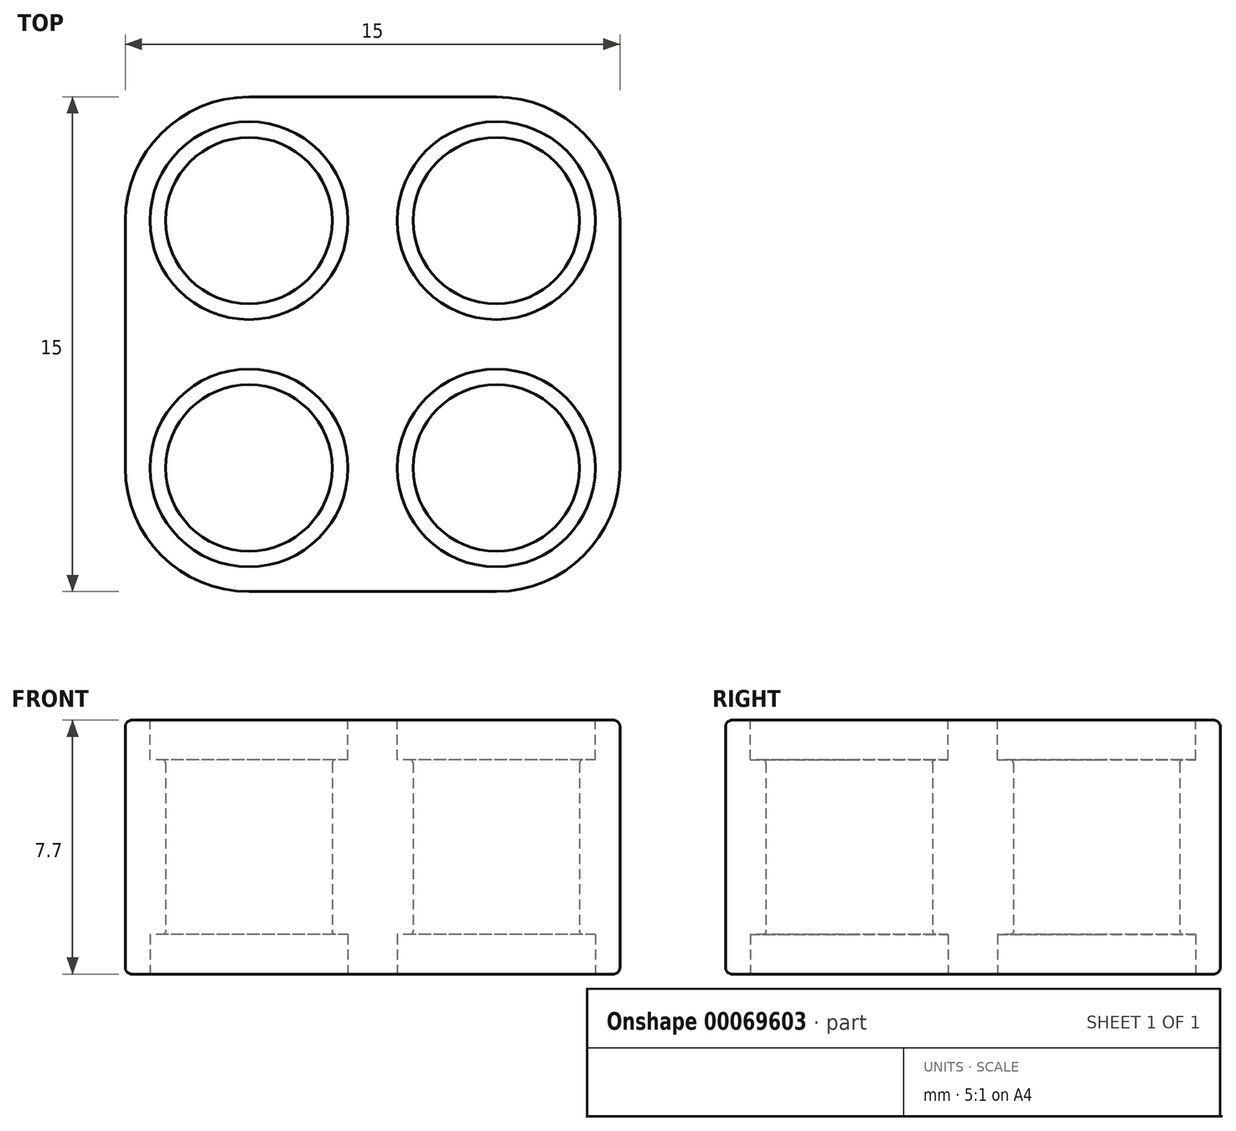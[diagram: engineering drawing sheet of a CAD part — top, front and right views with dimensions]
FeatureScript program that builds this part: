
annotation { "Feature Type Name" : "Feature", "Feature Type Description" : "" }
export const myFeature = defineFeature(function(context is Context, id is Id, definition is map)
    precondition{}
    {
        {
            var Q0;
            Q0=qCreatedBy(makeId("Top.planeOp"),FACE);
            var sketch = newSketch(context, id + "F0", { "sketchPlane" : qUnion([Q0])});
            skLineSegment(sketch, "E0.rect.bottom", {"start": v(3.75, -7.5) * mm, "end": v(-3.75, -7.5) * mm});
            skLineSegment(sketch, "E0.rect.top", {"start": v(3.75, 7.5) * mm, "end": v(-3.75, 7.5) * mm});
            skLineSegment(sketch, "E0.rect.left", {"start": v(7.5, -3.75) * mm, "end": v(7.5, 3.75) * mm});
            skLineSegment(sketch, "E0.rect.right", {"start": v(-7.5, -3.75) * mm, "end": v(-7.5, 3.75) * mm});
            skPoint(sketch, "E0.rect.middle", {"position": v(0, 0) * mm});
            skPoint(sketch, "E1.visualSharp", {"position": v(7.5, 7.5) * mm});
            skArc(sketch, "E1.filletArc", {"start": v(7.5, 3.75) * mm, "mid": v(6.4, 6.4) * mm, "end": v(3.75, 7.5) * mm});
            skPoint(sketch, "E2.visualSharp", {"position": v(-7.5, 7.5) * mm});
            skArc(sketch, "E2.filletArc", {"start": v(-3.75, 7.5) * mm, "mid": v(-6.4, 6.4) * mm, "end": v(-7.5, 3.75) * mm});
            skPoint(sketch, "E3.visualSharp", {"position": v(-7.5, -7.5) * mm});
            skArc(sketch, "E3.filletArc", {"start": v(-7.5, -3.75) * mm, "mid": v(-6.4, -6.4) * mm, "end": v(-3.75, -7.5) * mm});
            skPoint(sketch, "E4.visualSharp", {"position": v(7.5, -7.5) * mm});
            skArc(sketch, "E4.filletArc", {"start": v(3.75, -7.5) * mm, "mid": v(6.4, -6.4) * mm, "end": v(7.5, -3.75) * mm});
            skCircle(sketch, "E5", {"center": v(-3.75, 3.75) * mm, "radius": 2.52 * mm});
            skLineSegment(sketch, "E6", {"start": v(0, 0) * mm, "end": v(0, 7.5) * mm, "construction": true});
            skLineSegment(sketch, "E7", {"start": v(0, 0) * mm, "end": v(7.5, 0) * mm, "construction": true});
            skCircle(sketch, "E8.MirrorC", {"center": v(3.75, 3.75) * mm, "radius": 2.52 * mm});
            skCircle(sketch, "E9.MirrorC", {"center": v(3.75, -3.75) * mm, "radius": 2.52 * mm});
            skCircle(sketch, "E10.MirrorC", {"center": v(-3.75, -3.75) * mm, "radius": 2.52 * mm});
            skSolve(sketch);
        }
        {
            var Q0;
            Q0 = qSketchRegion(id + "F0", true);
            extrude(context, id + "F1", {"entities" : qUnion([Q0]), "depth" : 3.85 * mm});
        }
        {
            var Q0;
            Q0=makeQuery(id+"F1.opExtrude","CAP_FACE",FACE,{"disambiguationData":[OSD([sQuery(id+"F0.wireOp",EDGE,"E0.rect.bottom"),sQuery(id+"F0.wireOp",EDGE,"E0.rect.top"),sQuery(id+"F0.wireOp",EDGE,"E0.rect.left"),sQuery(id+"F0.wireOp",EDGE,"E0.rect.right"),sQuery(id+"F0.wireOp",EDGE,"E1.filletArc"),sQuery(id+"F0.wireOp",EDGE,"E2.filletArc"),sQuery(id+"F0.wireOp",EDGE,"E3.filletArc"),sQuery(id+"F0.wireOp",EDGE,"E4.filletArc"),sQuery(id+"F0.wireOp",EDGE,"E5"),sQuery(id+"F0.wireOp",EDGE,"E8.MirrorC"),sQuery(id+"F0.wireOp",EDGE,"E9.MirrorC"),sQuery(id+"F0.wireOp",EDGE,"E10.MirrorC")])],"isStart":false});
            fillet(context, id + "F2", {"entities" : qUnion([Q0]), "radius" : 0.2 * mm, "tangentPropagation" : true, "allowEdgeOverflow" : false});
        }
        {
            var Q0;
            Q0=makeQuery(id+"F1.opExtrude","CAP_FACE",FACE,{"disambiguationData":[OSD([sQuery(id+"F0.wireOp",EDGE,"E0.rect.bottom"),sQuery(id+"F0.wireOp",EDGE,"E0.rect.top"),sQuery(id+"F0.wireOp",EDGE,"E0.rect.left"),sQuery(id+"F0.wireOp",EDGE,"E0.rect.right"),sQuery(id+"F0.wireOp",EDGE,"E1.filletArc"),sQuery(id+"F0.wireOp",EDGE,"E2.filletArc"),sQuery(id+"F0.wireOp",EDGE,"E3.filletArc"),sQuery(id+"F0.wireOp",EDGE,"E4.filletArc"),sQuery(id+"F0.wireOp",EDGE,"E5"),sQuery(id+"F0.wireOp",EDGE,"E8.MirrorC"),sQuery(id+"F0.wireOp",EDGE,"E9.MirrorC"),sQuery(id+"F0.wireOp",EDGE,"E10.MirrorC")])],"isStart":false});
            var sketch = newSketch(context, id + "F3", { "sketchPlane" : qUnion([Q0])});
            skCircle(sketch, "E11", {"center": v(-3.75, 3.75) * mm, "radius": 3 * mm});
            skCircle(sketch, "E12.MirrorC", {"center": v(3.75, 3.75) * mm, "radius": 3 * mm});
            skCircle(sketch, "E13.MirrorC", {"center": v(3.75, -3.75) * mm, "radius": 3 * mm});
            skCircle(sketch, "E14.MirrorC", {"center": v(-3.75, -3.75) * mm, "radius": 3 * mm});
            skSolve(sketch);
        }
        {
            var Q0;
            Q0 = qSketchRegion(id + "F3", true);
            extrude(context, id + "F4", {"entities" : qUnion([Q0]), "operationType" : NewBodyOperationType.REMOVE, "oppositeDirection" : true, "depth" : 1.2 * mm});
        }
        {
            var Q0;
            Q0=makeQuery(id+"F4.boolean.opBoolean","COPY",EDGE,{"derivedFrom":makeQuery(id+"F4.opExtrude","CAP_EDGE",EDGE,{"disambiguationData":[OSD([sQuery(id+"F3.wireOp",EDGE,"E14.MirrorC")])],"isStart":true})});
            var Q1;
            Q1=makeQuery(id+"F4.boolean.opBoolean","INTERSECT",EDGE,{"derivedFrom":[makeQuery(id+"F1.opExtrude","SWEPT_FACE",FACE,{"disambiguationData":[OSD([sQuery(id+"F0.wireOp",EDGE,"E10.MirrorC")])]}),makeQuery(id+"F4.opExtrude","CAP_FACE",FACE,{"disambiguationData":[OSD([sQuery(id+"F3.wireOp",EDGE,"E14.MirrorC")])],"isStart":false})]});
            var Q2;
            Q2=makeQuery(id+"F4.boolean.opBoolean","COPY",EDGE,{"derivedFrom":makeQuery(id+"F4.opExtrude","CAP_EDGE",EDGE,{"disambiguationData":[OSD([sQuery(id+"F3.wireOp",EDGE,"E11")])],"isStart":true})});
            var Q3;
            Q3=makeQuery(id+"F4.boolean.opBoolean","INTERSECT",EDGE,{"derivedFrom":[makeQuery(id+"F1.opExtrude","SWEPT_FACE",FACE,{"disambiguationData":[OSD([sQuery(id+"F0.wireOp",EDGE,"E5")])]}),makeQuery(id+"F4.opExtrude","CAP_FACE",FACE,{"disambiguationData":[OSD([sQuery(id+"F3.wireOp",EDGE,"E11")])],"isStart":false})]});
            var Q4;
            Q4=makeQuery(id+"F4.boolean.opBoolean","COPY",EDGE,{"derivedFrom":makeQuery(id+"F4.opExtrude","CAP_EDGE",EDGE,{"disambiguationData":[OSD([sQuery(id+"F3.wireOp",EDGE,"E12.MirrorC")])],"isStart":true})});
            var Q5;
            Q5=makeQuery(id+"F4.boolean.opBoolean","INTERSECT",EDGE,{"derivedFrom":[makeQuery(id+"F1.opExtrude","SWEPT_FACE",FACE,{"disambiguationData":[OSD([sQuery(id+"F0.wireOp",EDGE,"E8.MirrorC")])]}),makeQuery(id+"F4.opExtrude","CAP_FACE",FACE,{"disambiguationData":[OSD([sQuery(id+"F3.wireOp",EDGE,"E12.MirrorC")])],"isStart":false})]});
            var Q6;
            Q6=makeQuery(id+"F4.boolean.opBoolean","INTERSECT",EDGE,{"derivedFrom":[makeQuery(id+"F1.opExtrude","SWEPT_FACE",FACE,{"disambiguationData":[OSD([sQuery(id+"F0.wireOp",EDGE,"E9.MirrorC")])]}),makeQuery(id+"F4.opExtrude","CAP_FACE",FACE,{"disambiguationData":[OSD([sQuery(id+"F3.wireOp",EDGE,"E13.MirrorC")])],"isStart":false})]});
            var Q7;
            Q7=makeQuery(id+"F4.boolean.opBoolean","COPY",EDGE,{"derivedFrom":makeQuery(id+"F4.opExtrude","CAP_EDGE",EDGE,{"disambiguationData":[OSD([sQuery(id+"F3.wireOp",EDGE,"E13.MirrorC")])],"isStart":true})});
            fillet(context, id + "F5", {"entities" : qUnion([Q0, Q1, Q2, Q3, Q4, Q5, Q6, Q7]), "radius" : 0.1 * mm, "tangentPropagation" : true, "allowEdgeOverflow" : false});
        }
        {
            var Q0;
            Q0=makeQuery(id+"F1.opExtrude","SWEPT_BODY",BODY,{"disambiguationData":[OSD([sQuery(id+"F0.wireOp",EDGE,"E0.rect.bottom"),sQuery(id+"F0.wireOp",EDGE,"E0.rect.top"),sQuery(id+"F0.wireOp",EDGE,"E0.rect.left"),sQuery(id+"F0.wireOp",EDGE,"E0.rect.right"),sQuery(id+"F0.wireOp",EDGE,"E1.filletArc"),sQuery(id+"F0.wireOp",EDGE,"E2.filletArc"),sQuery(id+"F0.wireOp",EDGE,"E3.filletArc"),sQuery(id+"F0.wireOp",EDGE,"E4.filletArc"),sQuery(id+"F0.wireOp",EDGE,"E5"),sQuery(id+"F0.wireOp",EDGE,"E8.MirrorC"),sQuery(id+"F0.wireOp",EDGE,"E9.MirrorC"),sQuery(id+"F0.wireOp",EDGE,"E10.MirrorC")])]});
            var Q1;
            Q1=qCreatedBy(makeId("Top.planeOp"),FACE);
            mirror(context, id + "F6", {"operationType" : NewBodyOperationType.ADD, "entities" : qUnion([Q0]), "mirrorPlane" : qUnion([Q1])});
        }
    });
